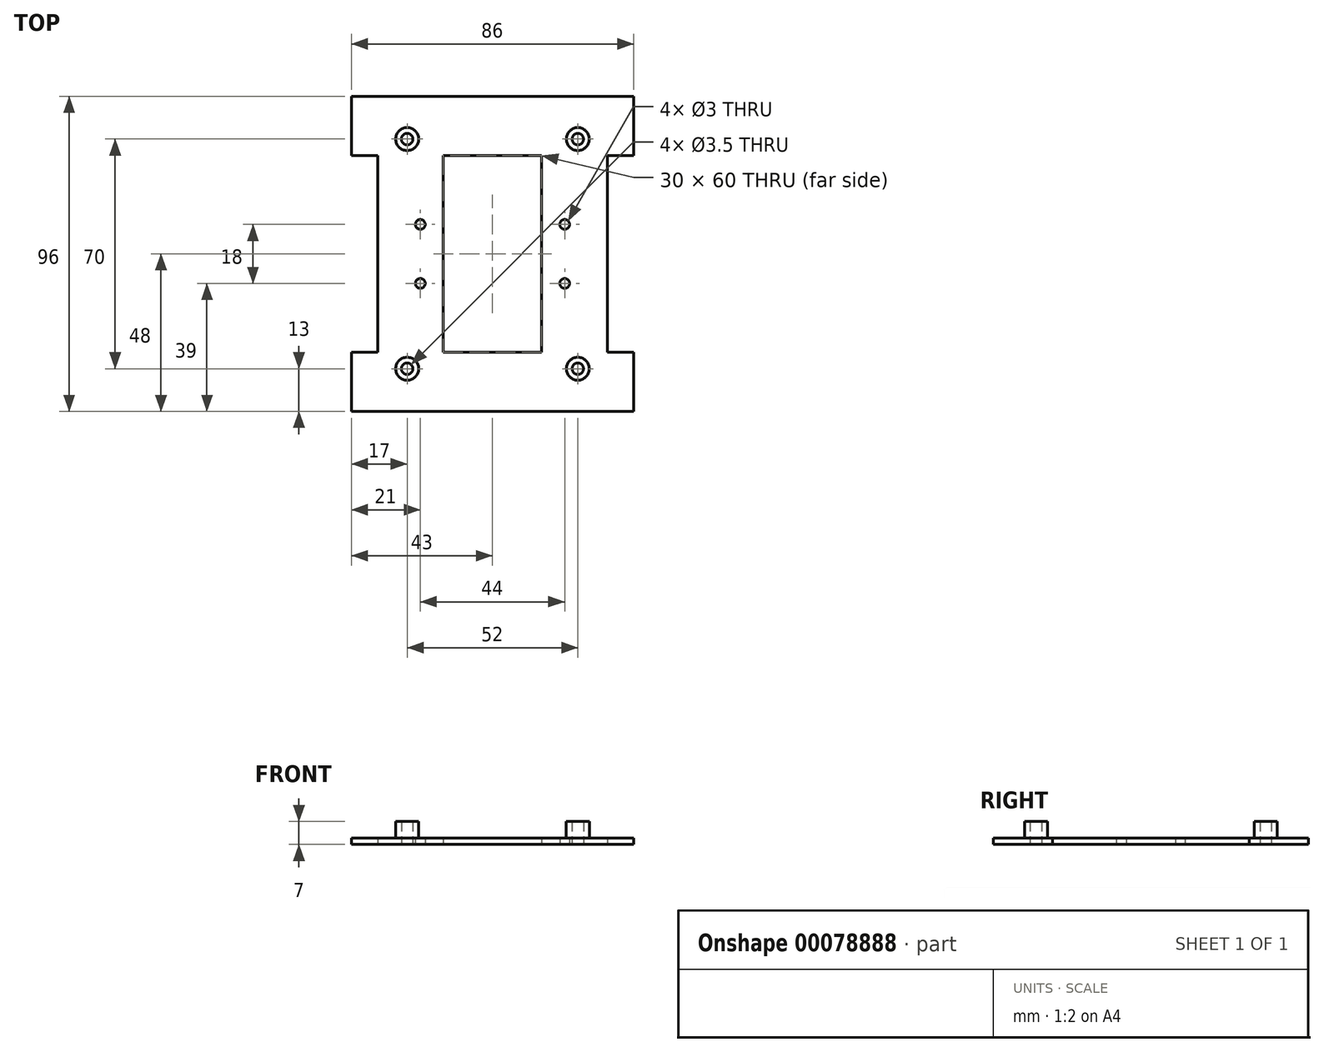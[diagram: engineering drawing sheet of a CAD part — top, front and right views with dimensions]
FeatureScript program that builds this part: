
annotation { "Feature Type Name" : "Feature", "Feature Type Description" : "" }
export const myFeature = defineFeature(function(context is Context, id is Id, definition is map)
    precondition{}
    {
        {
            var Q0;
            Q0=qCreatedBy(makeId("Top.planeOp"),FACE);
            var sketch = newSketch(context, id + "F0", { "sketchPlane" : qUnion([Q0])});
            skLineSegment(sketch, "E0.bottom", {"start": v(43, 48) * mm, "end": v(-43, 48) * mm});
            skLineSegment(sketch, "E0.top", {"start": v(43, -48) * mm, "end": v(-43, -48) * mm});
            skLineSegment(sketch, "E0.left", {"start": v(43, 48) * mm, "end": v(43, 30) * mm});
            skLineSegment(sketch, "E0.right", {"start": v(-43, 48) * mm, "end": v(-43, 30) * mm});
            skPoint(sketch, "E0.middle", {"position": v(0, 0) * mm});
            skLineSegment(sketch, "E1.bottom", {"start": v(-43, 48) * mm, "end": v(-35, 48) * mm});
            skLineSegment(sketch, "E1.top", {"start": v(-43, 30) * mm, "end": v(-35, 30) * mm});
            skLineSegment(sketch, "E1.right", {"start": v(-35, 48) * mm, "end": v(-35, 30) * mm, "construction": true});
            skLineSegment(sketch, "E2.bottom", {"start": v(43, 48) * mm, "end": v(35, 48) * mm});
            skLineSegment(sketch, "E2.top", {"start": v(43, 30) * mm, "end": v(35, 30) * mm});
            skLineSegment(sketch, "E2.right", {"start": v(35, 48) * mm, "end": v(35, 30) * mm, "construction": true});
            skLineSegment(sketch, "E3.bottom", {"start": v(43, -48) * mm, "end": v(35, -48) * mm});
            skLineSegment(sketch, "E3.top", {"start": v(43, -30) * mm, "end": v(35, -30) * mm});
            skLineSegment(sketch, "E3.left", {"start": v(43, -48) * mm, "end": v(43, -30) * mm});
            skLineSegment(sketch, "E3.right", {"start": v(35, -48) * mm, "end": v(35, -30) * mm, "construction": true});
            skLineSegment(sketch, "E4.bottom", {"start": v(-43, -48) * mm, "end": v(-35, -48) * mm});
            skLineSegment(sketch, "E4.top", {"start": v(-43, -30) * mm, "end": v(-35, -30) * mm});
            skLineSegment(sketch, "E4.left", {"start": v(-43, -48) * mm, "end": v(-43, -30) * mm});
            skLineSegment(sketch, "E4.right", {"start": v(-35, -48) * mm, "end": v(-35, -30) * mm, "construction": true});
            skLineSegment(sketch, "E5", {"start": v(-43, 30) * mm, "end": v(-43, -30) * mm, "construction": true});
            skLineSegment(sketch, "E6", {"start": v(-43, -30) * mm, "end": v(-43, -48) * mm});
            skLineSegment(sketch, "E7", {"start": v(43, -30) * mm, "end": v(43, -48) * mm});
            skLineSegment(sketch, "E8", {"start": v(43, 30) * mm, "end": v(43, -30) * mm, "construction": true});
            skLineSegment(sketch, "E9", {"start": v(-35, 30) * mm, "end": v(-35, 0) * mm});
            skLineSegment(sketch, "E10", {"start": v(35, 30) * mm, "end": v(35, 0) * mm});
            skLineSegment(sketch, "E11.bottom", {"start": v(15, 30) * mm, "end": v(-15, 30) * mm});
            skLineSegment(sketch, "E11.top", {"start": v(15, -30) * mm, "end": v(-15, -30) * mm});
            skLineSegment(sketch, "E11.left", {"start": v(15, 30) * mm, "end": v(15, -30) * mm});
            skLineSegment(sketch, "E11.right", {"start": v(-15, 30) * mm, "end": v(-15, -30) * mm});
            skLineSegment(sketch, "E12.bottom", {"start": v(-43, 48) * mm, "end": v(-26, 48) * mm, "construction": true});
            skLineSegment(sketch, "E12.top", {"start": v(-43, 35) * mm, "end": v(-26, 35) * mm, "construction": true});
            skLineSegment(sketch, "E12.left", {"start": v(-43, 48) * mm, "end": v(-43, 35) * mm, "construction": true});
            skLineSegment(sketch, "E12.right", {"start": v(-26, 48) * mm, "end": v(-26, 35) * mm, "construction": true});
            skLineSegment(sketch, "E13.bottom", {"start": v(43, 48) * mm, "end": v(26, 48) * mm, "construction": true});
            skLineSegment(sketch, "E13.top", {"start": v(43, 35) * mm, "end": v(26, 35) * mm, "construction": true});
            skLineSegment(sketch, "E13.left", {"start": v(43, 48) * mm, "end": v(43, 35) * mm, "construction": true});
            skLineSegment(sketch, "E13.right", {"start": v(26, 48) * mm, "end": v(26, 35) * mm, "construction": true});
            skLineSegment(sketch, "E14.bottom", {"start": v(43, -48) * mm, "end": v(26, -48) * mm, "construction": true});
            skLineSegment(sketch, "E14.top", {"start": v(43, -35) * mm, "end": v(26, -35) * mm, "construction": true});
            skLineSegment(sketch, "E14.left", {"start": v(43, -48) * mm, "end": v(43, -35) * mm, "construction": true});
            skLineSegment(sketch, "E14.right", {"start": v(26, -48) * mm, "end": v(26, -35) * mm, "construction": true});
            skLineSegment(sketch, "E15.bottom", {"start": v(-43, -48) * mm, "end": v(-26, -48) * mm, "construction": true});
            skLineSegment(sketch, "E15.top", {"start": v(-43, -35) * mm, "end": v(-26, -35) * mm, "construction": true});
            skLineSegment(sketch, "E15.left", {"start": v(-43, -48) * mm, "end": v(-43, -35) * mm, "construction": true});
            skLineSegment(sketch, "E15.right", {"start": v(-26, -48) * mm, "end": v(-26, -35) * mm, "construction": true});
            skCircle(sketch, "E16", {"center": v(-26, 35) * mm, "radius": 1.75 * mm});
            skCircle(sketch, "E17", {"center": v(26, 35) * mm, "radius": 1.75 * mm});
            skCircle(sketch, "E18", {"center": v(26, -35) * mm, "radius": 1.75 * mm});
            skCircle(sketch, "E19", {"center": v(-26, -35) * mm, "radius": 1.75 * mm});
            skLineSegment(sketch, "E20", {"start": v(-35, 0) * mm, "end": v(-35, -30) * mm});
            skLineSegment(sketch, "E21", {"start": v(35, 0) * mm, "end": v(35, -30) * mm});
            skLineSegment(sketch, "E22.bottom", {"start": v(-35, 0) * mm, "end": v(-22, 0) * mm, "construction": true});
            skLineSegment(sketch, "E22.top", {"start": v(-35, 9) * mm, "end": v(-22, 9) * mm, "construction": true});
            skLineSegment(sketch, "E22.left", {"start": v(-35, 0) * mm, "end": v(-35, 9) * mm, "construction": true});
            skLineSegment(sketch, "E22.right", {"start": v(-22, 0) * mm, "end": v(-22, 9) * mm, "construction": true});
            skLineSegment(sketch, "E23.top", {"start": v(-35, -9) * mm, "end": v(-22, -9) * mm, "construction": true});
            skLineSegment(sketch, "E23.left", {"start": v(-35, 0) * mm, "end": v(-35, -9) * mm, "construction": true});
            skLineSegment(sketch, "E23.right", {"start": v(-22, 0) * mm, "end": v(-22, -9) * mm, "construction": true});
            skLineSegment(sketch, "E24.bottom", {"start": v(35, 0) * mm, "end": v(22, 0) * mm, "construction": true});
            skLineSegment(sketch, "E24.top", {"start": v(35, 9) * mm, "end": v(22, 9) * mm, "construction": true});
            skLineSegment(sketch, "E24.left", {"start": v(35, 0) * mm, "end": v(35, 9) * mm, "construction": true});
            skLineSegment(sketch, "E24.right", {"start": v(22, 0) * mm, "end": v(22, 9) * mm, "construction": true});
            skLineSegment(sketch, "E25.top", {"start": v(35, -9) * mm, "end": v(22, -9) * mm, "construction": true});
            skLineSegment(sketch, "E25.left", {"start": v(35, 0) * mm, "end": v(35, -9) * mm, "construction": true});
            skLineSegment(sketch, "E25.right", {"start": v(22, 0) * mm, "end": v(22, -9) * mm, "construction": true});
            skCircle(sketch, "E26", {"center": v(-22, 9) * mm, "radius": 1.5 * mm});
            skCircle(sketch, "E27", {"center": v(-22, -9) * mm, "radius": 1.5 * mm});
            skCircle(sketch, "E28", {"center": v(22, 9) * mm, "radius": 1.5 * mm});
            skCircle(sketch, "E29", {"center": v(22, -9) * mm, "radius": 1.5 * mm});
            skCircle(sketch, "E30", {"center": v(-26, 35) * mm, "radius": 3.5 * mm});
            skCircle(sketch, "E31", {"center": v(26, 35) * mm, "radius": 3.5 * mm});
            skCircle(sketch, "E32", {"center": v(26, -35) * mm, "radius": 3.5 * mm});
            skCircle(sketch, "E33", {"center": v(-26, -35) * mm, "radius": 3.5 * mm});
            skSolve(sketch);
        }
        {
            var Q0;
            Q0=makeQuery(id+"F0.imprint","IMPRINT",FACE,{"disambiguationData":[TD([[makeQuery(id+"F0.imprint","IMPRINT",EDGE,{"derivedFrom":sQuery(id+"F0.wireOp",EDGE,"E0.bottom")}),1.0]])]});
            extrude(context, id + "F1", {"entities" : qUnion([Q0]), "depth" : 2 * mm});
        }
        {
            var Q0;
            Q0=makeQuery(id+"F0.imprint","IMPRINT",FACE,{"disambiguationData":[TD([[makeQuery(id+"F0.imprint","IMPRINT",EDGE,{"derivedFrom":sQuery(id+"F0.wireOp",EDGE,"E16")}),-1.0]])]});
            var Q1;
            Q1=makeQuery(id+"F0.imprint","IMPRINT",FACE,{"disambiguationData":[TD([[makeQuery(id+"F0.imprint","IMPRINT",EDGE,{"derivedFrom":sQuery(id+"F0.wireOp",EDGE,"E17")}),-1.0]])]});
            var Q2;
            Q2=makeQuery(id+"F0.imprint","IMPRINT",FACE,{"disambiguationData":[TD([[makeQuery(id+"F0.imprint","IMPRINT",EDGE,{"derivedFrom":sQuery(id+"F0.wireOp",EDGE,"E18")}),-1.0]])]});
            var Q3;
            Q3=makeQuery(id+"F0.imprint","IMPRINT",FACE,{"disambiguationData":[TD([[makeQuery(id+"F0.imprint","IMPRINT",EDGE,{"derivedFrom":sQuery(id+"F0.wireOp",EDGE,"E19")}),-1.0]])]});
            extrude(context, id + "F2", {"entities" : qUnion([Q0, Q1, Q2, Q3]), "operationType" : NewBodyOperationType.ADD, "depth" : 7 * mm});
        }
    });
